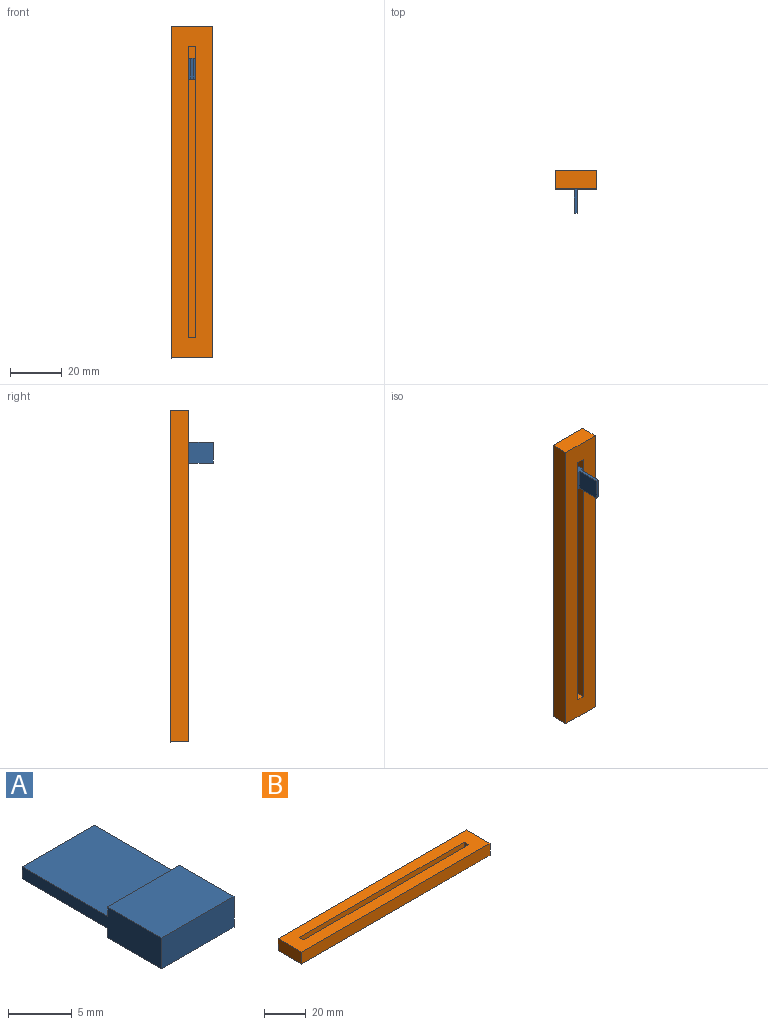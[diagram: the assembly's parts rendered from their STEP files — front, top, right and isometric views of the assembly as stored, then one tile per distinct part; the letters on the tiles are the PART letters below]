
ASSEMBLY  parts=2 mates=1
PART A: 10 faces, bbox 8x15.5x3 mm
  f0: plane 8x6mm, normal (0,0,-1), area 48mm2, adj f2,f3,f4,f8
  f1: plane 8x1.15mm, normal (0,1,0), area 9.2mm2, adj f2,f3,f7,f9
  f2: plane 15.5x2.95mm, normal (-1,0,0), area 28.6mm2, adj f0,f1,f4,f5,f6,f7,f8,f9
  f3: plane 15.5x2.95mm, normal (1,0,0), area 28.6mm2, adj f0,f1,f4,f5,f6,f7,f8,f9
  f4: plane 8x2.95mm, normal (0,-1,0), area 23.6mm2, adj f0,f2,f3,f5
  f5: plane 8x6mm, normal (0,0,1), area 48mm2, adj f2,f3,f4,f6
  f6: plane 8x0.9mm, normal (0,1,0), area 7.2mm2, adj f2,f3,f5,f7
  f7: plane 9.5x8mm, normal (0,0,1), area 76mm2, adj f1,f2,f3,f6
  f8: plane 8x0.9mm, normal (0,1,0), area 7.2mm2, adj f0,f2,f3,f9
  f9: plane 9.5x8mm, normal (0,0,-1), area 76mm2, adj f1,f2,f3,f8
PART B: 11 faces, bbox 128x16x7 mm
  f0: plane 128x7mm, normal (0,1,0), area 896mm2, adj f1,f3,f4,f5
  f1: plane 16x7mm, normal (-1,0,0), area 112mm2, adj f0,f2,f4,f5
  f2: plane 128x7mm, normal (0,-1,0), area 896mm2, adj f1,f3,f4,f5
  f3: plane 16x7mm, normal (1,0,0), area 112mm2, adj f0,f2,f4,f5
  f4: plane 128x16mm, normal (0,0,1), area 1712mm2, adj f0,f1,f2,f3,f6,f7,f8,f9
  f5: plane 128x16mm, normal (0,0,-1), area 2048mm2, adj f0,f1,f2,f3
  f6: plane 6x3mm, normal (1,0,0), area 18mm2, adj f4,f7,f9,f10
  f7: plane 112x6mm, normal (0,1,0), area 672mm2, adj f4,f6,f8,f10
  f8: plane 6x3mm, normal (-1,0,0), area 18mm2, adj f4,f7,f9,f10
  f9: plane 112x6mm, normal (0,-1,0), area 672mm2, adj f4,f6,f8,f10
  f10: plane 112x3mm, normal (0,0,1), area 336mm2, adj f6,f7,f8,f9
PLACE A rot(axis=(-0.71,0,0.71),180deg) t=(132.13,80.28,117.11)mm
PLACE B rot(axis=(0.58,0.58,-0.58),120deg) t=(130.68,81.28,69.57)mm
MATE slider B.f8 <-> A.f2  axis (0,0,-1) through (129.18,80.28,13.57)mm
